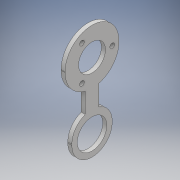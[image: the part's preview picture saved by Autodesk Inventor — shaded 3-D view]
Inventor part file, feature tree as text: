
AUTODESK INVENTOR PART (.ipt)
format: ipt  version: 2017 SP1 (Build 210196100, 196)  size: 336,384 bytes
history: native  units: mm
features: sketch x6, extrude x4, fillet x3, hole x2
ambient origin geometry x8: Origin, YZ Plane, XZ Plane, XY Plane, X Axis, Y Axis, Z Axis, Center Point
bodies: Solide1 (feature_tree)
feature tree (15):
  extrude  "Extrusion1"  Depth=60.0mm
  extrude  "Extrusion2"  Depth=10.0mm
  extrude  "Extrusion3"  Depth=5.0mm
  hole  "Perçage1"  [1 undecoded]
  fillet  "Congé1"  Radius=49.2442mm
  fillet  "Congé2"  Radius=5.0mm
  extrude  "Extrusion4"  Depth=3.0mm TaperAngle=0.0deg
  hole  "Perçage2"  [1 undecoded]
  fillet  "Congé3"  Radius=25.0mm
  sketch  "Esquisse1"
  sketch  "Esquisse2"
  sketch  "Esquisse3"
  sketch  "Esquisse4"
  sketch  "Esquisse5"
  sketch  "Esquisse6"
note: 2 required parameter values undecoded (feature->parameter linkage not recoverable at this tier; creation-order binding heuristic only, values carry confidence <= 0.55)
